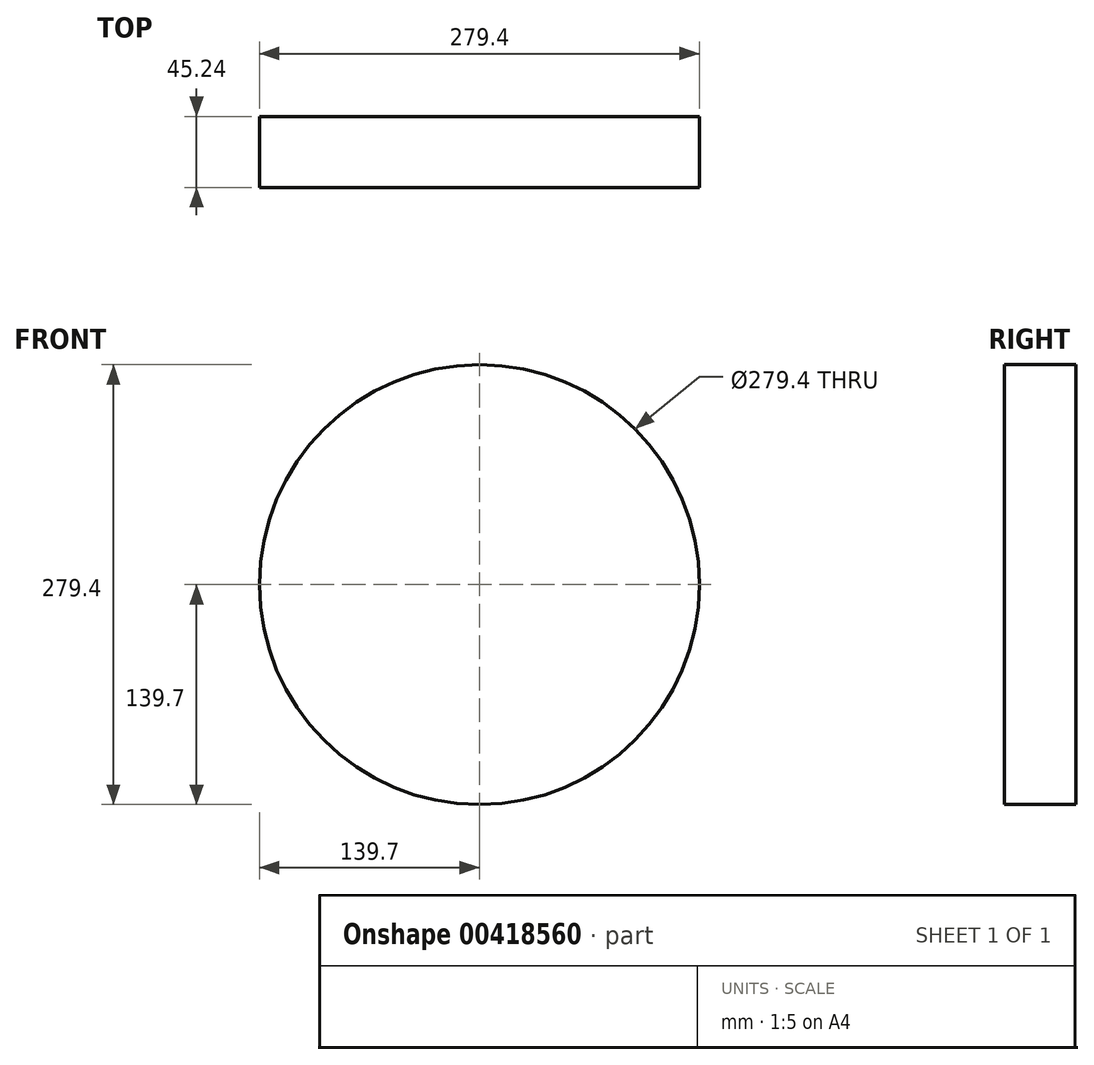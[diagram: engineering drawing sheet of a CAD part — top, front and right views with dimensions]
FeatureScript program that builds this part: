
annotation { "Feature Type Name" : "Feature", "Feature Type Description" : "" }
export const myFeature = defineFeature(function(context is Context, id is Id, definition is map)
    precondition{}
    {
        {
            var Q0;
            Q0=qCreatedBy(makeId("Front.planeOp"),FACE);
            var sketch = newSketch(context, id + "F0", { "sketchPlane" : qUnion([Q0])});
            skCircle(sketch, "E0", {"center": v(0, 0) * mm, "radius": 139.7 * mm});
            skSolve(sketch);
        }
        {
            var Q0;
            Q0 = qSketchRegion(id + "F0", true);
            var Q1;
            Q1=makeQuery(id+"F0.imprint","IMPRINT",FACE,{"disambiguationData":[TD([[makeQuery(id+"F0.imprint","IMPRINT",EDGE,{"derivedFrom":sQuery(id+"F0.wireOp",EDGE,"E0")}),1.0]])]});
            var Q2;
            Q2=sQuery(id+"F0.wireOp",EDGE,"E0");
            extrude(context, id + "F1", {"entities" : qUnion([Q0, Q1]), "bodyType" : ToolBodyType.SURFACE, "surfaceEntities" : qUnion([Q2]), "oppositeDirection" : true, "depth" : 45.24 * mm});
        }
    });
